FCSTD DOCUMENT  (FreeCAD 0.16R6706 (Git))
Label: coxa
License: All rights reserved
LicenseURL: http://en.wikipedia.org/wiki/All_rights_reserved
objects: Sketcher::SketchObject×3
note: 3 computed .brp shape members not serialized (recipe doc carries the construction recipe); baked Part::Feature solids carry a one-line shape summary decoded from their .brp

FEATURE [Sketcher::SketchObject] Sketch  label="coxa_up"
  sketch-geometry (27):
    g0: LineSegment StartX=38.0826 StartY=27.4348 StartZ=0 EndX=51.0826 EndY=27.4348 EndZ=0
    g1: LineSegment StartX=38.0826 StartY=11.9348 StartZ=0 EndX=51.0826 EndY=11.9348 EndZ=0
    g2: LineSegment StartX=65.8826 StartY=27.4348 StartZ=0 EndX=65.8826 EndY=30.4348 EndZ=0
    g3: LineSegment StartX=65.8826 StartY=30.4348 StartZ=0 EndX=68.8826 EndY=30.4348 EndZ=0
    g4: LineSegment StartX=68.8826 StartY=30.4348 StartZ=0 EndX=68.8826 EndY=8.93483 EndZ=0
    g5: LineSegment StartX=68.8826 StartY=8.93483 StartZ=0 EndX=65.8826 EndY=8.93483 EndZ=0
    g6: LineSegment StartX=65.8826 StartY=8.93483 StartZ=0 EndX=65.8826 EndY=11.9348 EndZ=0
    g7: LineSegment StartX=65.8826 StartY=11.9348 StartZ=0 EndX=54.0826 EndY=11.9348 EndZ=0
    g8: LineSegment StartX=54.0826 StartY=11.9348 StartZ=0 EndX=54.0826 EndY=8.93483 EndZ=0
    g9: LineSegment StartX=54.0826 StartY=8.93483 StartZ=0 EndX=51.0826 EndY=8.93483 EndZ=0
    g10: LineSegment StartX=51.0826 StartY=8.93483 StartZ=0 EndX=51.0826 EndY=11.9348 EndZ=0
    g11: LineSegment StartX=51.0826 StartY=27.4348 StartZ=0 EndX=51.0826 EndY=30.4348 EndZ=0
    g12: LineSegment StartX=51.0826 StartY=30.4348 StartZ=0 EndX=54.0826 EndY=30.4348 EndZ=0
    g13: LineSegment StartX=54.0826 StartY=30.4348 StartZ=0 EndX=54.0826 EndY=27.4348 EndZ=0
    g14: LineSegment StartX=54.0826 StartY=27.4348 StartZ=0 EndX=65.8826 EndY=27.4348 EndZ=0
    g15: GeomPoint [constr] X=68.8826 Y=19.6848 Z=0
    g16: LineSegment [constr] StartX=68.8826 StartY=19.6848 StartZ=0 EndX=38.0826 EndY=19.6848 EndZ=0
    g17: ArcOfEllipse CenterX=38.0826 CenterY=19.6848 CenterZ=0 NormalX=0 NormalY=0 NormalZ=1 MajorRadius=11 MinorRadius=7.75 AngleXU=0 StartAngle=1.5708 EndAngle=4.71239
    g18: LineSegment [constr] StartX=49.0826 StartY=19.6848 StartZ=0 EndX=27.0826 EndY=19.6848 EndZ=0
    g19: LineSegment [constr] StartX=38.0826 StartY=27.4348 StartZ=0 EndX=38.0826 EndY=11.9348 EndZ=0
    g20: GeomPoint [constr] X=45.8888 Y=19.6848 Z=0
    g21: GeomPoint [constr] X=30.2764 Y=19.6848 Z=0
    g22: Circle CenterX=38.0826 CenterY=19.6848 CenterZ=0 NormalX=0 NormalY=0 NormalZ=1 Radius=3.5
    g23: Circle CenterX=31.0826 CenterY=19.6848 CenterZ=0 NormalX=0 NormalY=0 NormalZ=1 Radius=1.2
    g24: Circle CenterX=45.0826 CenterY=19.6848 CenterZ=0 NormalX=0 NormalY=0 NormalZ=1 Radius=1.2
    g25: GeomPoint [constr] X=59.9826 Y=27.4348 Z=0
    g26: LineSegment [constr] StartX=59.9826 StartY=27.4348 StartZ=0 EndX=59.9826 EndY=11.9348 EndZ=0
  constraints (66):
    c: Horizontal(g0)
    c: Horizontal(g1)
    c: Vertical(g2)
    c: Distance(g2,g0) = 3
    c: Coincident(g3,g2)
    c: Horizontal(g3)
    c: Distance(g3,g2) = 3
    c: Coincident(g4,g3)
    c: Vertical(g4)
    c: Horizontal(g5)
    c: Coincident(g6,g5)
    c: Vertical(g6)
    c: Horizontal(g7)
    c: Distance(g7,g6) = 11.8
    c: Vertical(g8)
    c: Coincident(g9,g8)
    c: Horizontal(g9)
    c: Distance(g9,g8) = 3
    c: Coincident(g10,g9)
    c: Vertical(g10)
    c: Coincident(g7,g8)
    c: Distance(g8,g7) = 3
    c: Distance(g5,g7) = 3
    c: Coincident(g1,g10)
    c: Vertical(g11)
    c: Coincident(g12,g11)
    c: Horizontal(g12)
    c: Distance(g12,g11) = 3
    c: Coincident(g13,g12)
    c: Vertical(g13)
    c: Coincident(g11,g0)
    c: Distance(g13,g2) = 11.8
    c: Coincident(g6,g7)
    c: Distance(g11,g0) = 3
    c: Coincident(g14,g13)
    c: Coincident(g14,g2)
    c: Horizontal(g14)
    c: Distance(g12,g14) = 3
    c: Distance(g9,g1) = 3
    c: Coincident(g16,g15)
    c: Horizontal(g16)
    c: InternalAlignment(g18-g21 -> g17) x4
    c: Coincident(g17,g16)
    c: Coincident(g0,g19)
    c: Coincident(g1,g19)
    c: Vertical(g19)
    c: PointOnObject(g17,g19)
    c: PointOnObject(g17,g19)
    c: Radius(g22) = 3.5
    c: PointOnObject(g23,g18)
    c: Radius(g23) = 1.2
    c: Coincident(g16,g22)
    c: Distance(g23,g16) = 7
    c: PointOnObject(g24,g16)
    c: Radius(g24) = 1.2
    c: Distance(g24,g16) = 7
    c: Symmetric(g13,g2,g25)
    c: Coincident(g26,g25)
    c: PointOnObject(g26,g7)
    c: Vertical(g26)
    c: Coincident(g4,g5)
    c: Distance(g6,g4) = 3
    c: PointOnObject(g15,g4)
    c: Distance(g13,g7) = 15.5
    c: Distance(g23,g18) = 4
    c: Distance(g0,g0) = 13
FEATURE [Sketcher::SketchObject] Sketch005  label="coxa_down"
  sketch-geometry (23):
    g0: LineSegment StartX=66.5079 StartY=3.73245 StartZ=0 EndX=66.5079 EndY=6.73245 EndZ=0
    g1: LineSegment StartX=66.5079 StartY=6.73245 StartZ=0 EndX=69.5079 EndY=6.73245 EndZ=0
    g2: LineSegment StartX=69.5079 StartY=6.73245 StartZ=0 EndX=69.5079 EndY=-14.7675 EndZ=0
    g3: LineSegment StartX=69.5079 StartY=-14.7675 StartZ=0 EndX=66.5079 EndY=-14.7675 EndZ=0
    g4: LineSegment StartX=66.5079 StartY=-14.7675 StartZ=0 EndX=66.5079 EndY=-11.7675 EndZ=0
    g5: LineSegment StartX=66.5079 StartY=-11.7675 StartZ=0 EndX=54.7079 EndY=-11.7675 EndZ=0
    g6: LineSegment StartX=54.7079 StartY=-11.7675 StartZ=0 EndX=54.7079 EndY=-14.7675 EndZ=0
    g7: LineSegment StartX=54.7079 StartY=-14.7675 StartZ=0 EndX=51.7079 EndY=-14.7675 EndZ=0
    g8: LineSegment StartX=51.7079 StartY=-14.7675 StartZ=0 EndX=51.7079 EndY=-11.7675 EndZ=0
    g9: LineSegment StartX=51.7079 StartY=3.73245 StartZ=0 EndX=51.7079 EndY=6.73245 EndZ=0
    g10: LineSegment StartX=51.7079 StartY=6.73245 StartZ=0 EndX=54.7079 EndY=6.73245 EndZ=0
    g11: LineSegment StartX=54.7079 StartY=6.73245 StartZ=0 EndX=54.7079 EndY=3.73245 EndZ=0
    g12: LineSegment StartX=54.7079 StartY=3.73245 StartZ=0 EndX=66.5079 EndY=3.73245 EndZ=0
    g13: GeomPoint [constr] X=51.7079 Y=3.73245 Z=0
    g14: LineSegment [constr] StartX=69.5079 StartY=-4.01755 StartZ=0 EndX=38.7079 EndY=-4.01755 EndZ=0
    g15: Circle CenterX=38.7079 CenterY=-4.01755 CenterZ=0 NormalX=0 NormalY=0 NormalZ=1 Radius=1.5
    g16: LineSegment [constr] StartX=51.7079 StartY=3.73245 StartZ=0 EndX=51.7079 EndY=-4.01755 EndZ=0
    g17: ArcOfEllipse CenterX=51.7079 CenterY=-4.01755 CenterZ=0 NormalX=0 NormalY=0 NormalZ=1 MajorRadius=17 MinorRadius=7.75 AngleXU=0 StartAngle=1.5708 EndAngle=4.71239
    g18: LineSegment [constr] StartX=68.7079 StartY=-4.01755 StartZ=0 EndX=34.7079 EndY=-4.01755 EndZ=0
    g19: LineSegment [constr] StartX=51.7079 StartY=3.73245 StartZ=0 EndX=51.7079 EndY=-11.7675 EndZ=0
    g20: GeomPoint [constr] X=36.5772 Y=-4.01755 Z=0
    g21: GeomPoint [constr] X=60.6079 Y=3.73245 Z=0
    g22: LineSegment [constr] StartX=60.6079 StartY=3.73245 StartZ=0 EndX=60.6079 EndY=-11.7675 EndZ=0
  constraints (66):
    c: Vertical(g0)
    c: Coincident(g1,g0)
    c: Horizontal(g1)
    c: Distance(g1,g0) = 3
    c: Vertical(g2)
    c: Horizontal(g3)
    c: Distance(g3,g2) = 3
    c: Coincident(g4,g3)
    c: Vertical(g4)
    c: Horizontal(g5)
    c: Distance(g5,g4) = 11.8
    c: Vertical(g6)
    c: Coincident(g7,g6)
    c: Horizontal(g7)
    c: Distance(g7,g6) = 3
    c: Coincident(g8,g7)
    c: Vertical(g8)
    c: Coincident(g5,g6)
    c: Distance(g6,g5) = 3
    c: Distance(g3,g5) = 3
    c: Vertical(g9)
    c: Coincident(g10,g9)
    c: Horizontal(g10)
    c: Distance(g10,g9) = 3
    c: Coincident(g11,g10)
    c: Vertical(g11)
    c: Distance(g11,g0) = 11.8
    c: Coincident(g4,g5)
    c: Coincident(g12,g0)
    c: Distance(g10,g12) = 3
    c: Coincident(g3,g2)
    c: Horizontal(g14)
    c: Radius(g15) = 1.5
    c: Coincident(g14,g15)
    c: Coincident(g16,g13)
    c: PointOnObject(g16,g14)
    c: Vertical(g16)
    c: InternalAlignment(g18,g17)
    c: InternalAlignment(g19,g17)
    c: InternalAlignment(g20,g17)
    c: Coincident(g19,g13)
    c: Vertical(g19)
    c: PointOnObject(g17,g16)
    c: PointOnObject(g17,g19)
    c: Tangent(g17,g17)
    c: PointOnObject(g16,g18)
    c: Tangent(g17,g17)
    c: PointOnObject(g8,g5)
    c: Distance(g14,g16) = 13
    c: PointOnObject(g10,g1)
    c: Symmetric(g11,g0,g21)
    c: PointOnObject(g12,g11)
    c: Coincident(g22,g21)
    c: PointOnObject(g22,g5)
    c: Vertical(g22)
    c: Tangent(g17,g17)
    c: Horizontal(g12)
    c: Coincident(g1,g2)
    c: PointOnObject(g14,g2)
    c: PointOnObject(g9,g12)
    c: PointOnObject(g11,g12)
    c: Distance(g11,g5) = 15.5
    c: PointOnObject(g13,g12)
    c: PointOnObject(g13,g9)
    c: PointOnObject(g17,g5)
    c: Distance(g14,g18) = 4
FEATURE [Sketcher::SketchObject] Sketch006  label="coxa_joint"
  sketch-geometry (35):
    g0: LineSegment StartX=97.0509 StartY=-32.2316 StartZ=0 EndX=85.2509 EndY=-32.2316 EndZ=0
    g1: LineSegment StartX=85.2509 StartY=-32.2316 StartZ=0 EndX=85.2509 EndY=-54.7316 EndZ=0
    g2: LineSegment StartX=85.2509 StartY=-54.7316 StartZ=0 EndX=97.0509 EndY=-54.7316 EndZ=0
    g3: LineSegment StartX=97.0509 StartY=-54.7316 StartZ=0 EndX=97.0509 EndY=-32.2316 EndZ=0
    g4: Circle CenterX=91.1509 CenterY=-29.2316 CenterZ=0 NormalX=0 NormalY=0 NormalZ=1 Radius=1.5
    g5: Circle CenterX=91.1509 CenterY=-57.7316 CenterZ=0 NormalX=0 NormalY=0 NormalZ=1 Radius=1.5
    g6: LineSegment StartX=97.0509 StartY=-23.2316 StartZ=0 EndX=100.051 EndY=-23.2316 EndZ=0
    g7: LineSegment StartX=100.051 StartY=-26.2316 StartZ=0 EndX=97.0509 EndY=-26.2316 EndZ=0
    g8: LineSegment StartX=97.0509 StartY=-26.2316 StartZ=0 EndX=97.0509 EndY=-23.2316 EndZ=0
    g9: LineSegment StartX=82.2509 StartY=-23.2316 StartZ=0 EndX=85.2509 EndY=-23.2316 EndZ=0
    g10: LineSegment StartX=85.2509 StartY=-23.2316 StartZ=0 EndX=85.2509 EndY=-26.2316 EndZ=0
    g11: LineSegment StartX=85.2509 StartY=-26.2316 StartZ=0 EndX=82.2509 EndY=-26.2316 EndZ=0
    g12: LineSegment StartX=97.0509 StartY=-60.7316 StartZ=0 EndX=100.051 EndY=-60.7316 EndZ=0
    g13: LineSegment StartX=100.051 StartY=-63.7316 StartZ=0 EndX=97.0509 EndY=-63.7316 EndZ=0
    g14: LineSegment StartX=97.0509 StartY=-63.7316 StartZ=0 EndX=97.0509 EndY=-60.7316 EndZ=0
    g15: LineSegment StartX=82.2509 StartY=-60.7316 StartZ=0 EndX=85.2509 EndY=-60.7316 EndZ=0
    g16: LineSegment StartX=85.2509 StartY=-60.7316 StartZ=0 EndX=85.2509 EndY=-63.7316 EndZ=0
    g17: LineSegment StartX=85.2509 StartY=-63.7316 StartZ=0 EndX=82.2509 EndY=-63.7316 EndZ=0
    g18: LineSegment StartX=85.2509 StartY=-20.2316 StartZ=0 EndX=97.0509 EndY=-20.2316 EndZ=0
    g19: LineSegment StartX=97.0509 StartY=-66.7316 StartZ=0 EndX=85.2509 EndY=-66.7316 EndZ=0
    g20: LineSegment [constr] StartX=85.2509 StartY=-32.2316 StartZ=0 EndX=97.0509 EndY=-32.2316 EndZ=0
    g21: LineSegment [constr] StartX=97.0509 StartY=-32.2316 StartZ=0 EndX=97.0509 EndY=-27.5316 EndZ=0
    g22: LineSegment [constr] StartX=97.0509 StartY=-27.5316 StartZ=0 EndX=85.2509 EndY=-27.5316 EndZ=0
    g23: LineSegment [constr] StartX=85.2509 StartY=-27.5316 StartZ=0 EndX=85.2509 EndY=-32.2316 EndZ=0
    g24: LineSegment [constr] StartX=91.1509 StartY=-29.2316 StartZ=0 EndX=91.1509 EndY=-57.7316 EndZ=0
    g25: GeomPoint [constr] X=91.1509 Y=-32.2316 Z=0
    g26: LineSegment [constr] StartX=100.051 StartY=-23.2316 StartZ=0 EndX=100.051 EndY=-63.7316 EndZ=0
    g27: ArcOfCircle CenterX=97.0509 CenterY=-23.2316 CenterZ=0 NormalX=0 NormalY=0 NormalZ=1 Radius=3 StartAngle=0 EndAngle=1.5708
    g28: ArcOfCircle CenterX=97.0509 CenterY=-63.7316 CenterZ=0 NormalX=0 NormalY=0 NormalZ=1 Radius=3 StartAngle=4.71239 EndAngle=6.28319
    g29: LineSegment StartX=100.051 StartY=-26.2316 StartZ=0 EndX=100.051 EndY=-60.7316 EndZ=0
    g30: LineSegment [constr] StartX=82.2509 StartY=-63.7316 StartZ=0 EndX=82.2509 EndY=-23.2316 EndZ=0
    g31: ArcOfCircle CenterX=85.2509 CenterY=-63.7316 CenterZ=0 NormalX=0 NormalY=0 NormalZ=1 Radius=3 StartAngle=3.14159 EndAngle=4.71239
    g32: ArcOfCircle CenterX=85.2509 CenterY=-23.2316 CenterZ=0 NormalX=0 NormalY=0 NormalZ=1 Radius=3 StartAngle=1.5708 EndAngle=3.14159
    g33: LineSegment StartX=82.2509 StartY=-26.2316 StartZ=0 EndX=82.2509 EndY=-60.7316 EndZ=0
    g34: GeomPoint [constr] X=91.1509 Y=-38.1316 Z=0
  constraints (101):
    c: Coincident(g0,g1)
    c: Coincident(g1,g2)
    c: Coincident(g2,g3)
    c: Coincident(g3,g0)
    c: Horizontal(g0)
    c: Horizontal(g2)
    c: Vertical(g1)
    c: Vertical(g3)
    c: Distance(g0,g3) = 11.8
    c: Distance(g0,g2) = 22.5
    c: Radius(g4) = 1.5
    c: Distance(g4,g0) = 3
    c: Radius(g5) = 1.5
    c: Distance(g5,g2) = 3
    c: Coincident(g7,g8)
    c: Coincident(g8,g6)
    c: Horizontal(g6)
    c: Horizontal(g7)
    c: Vertical(g8)
    c: Distance(g7,g6) = 3
    c: Coincident(g9,g10)
    c: Coincident(g10,g11)
    c: Horizontal(g9)
    c: Horizontal(g11)
    c: Vertical(g10)
    c: Distance(g10,g9) = 3
    c: Distance(g11,g10) = 3
    c: PointOnObject(g7,g3)
    c: PointOnObject(g10,g1)
    c: Distance(g7,g0) = 6
    c: Distance(g10,g0) = 6
    c: Coincident(g13,g14)
    c: Coincident(g14,g12)
    c: Horizontal(g12)
    c: Horizontal(g13)
    c: Vertical(g14)
    c: Distance(g13,g12) = 3
    c: PointOnObject(g12,g3)
    c: Distance(g12,g2) = 6
    c: Coincident(g15,g16)
    c: Coincident(g16,g17)
    c: Horizontal(g15)
    c: Horizontal(g17)
    c: Vertical(g16)
    c: Distance(g16,g15) = 3
    c: Distance(g17,g16) = 3
    c: PointOnObject(g15,g1)
    c: Distance(g15,g2) = 6
    c: Horizontal(g18)
    c: Horizontal(g19)
    c: Distance(g9,g18) = 3
    c: Distance(g13,g19) = 3
    c: Coincident(g20,g21)
    c: Coincident(g21,g22)
    c: Coincident(g22,g23)
    c: Coincident(g23,g20)
    c: Horizontal(g20)
    c: Horizontal(g22)
    c: Vertical(g21)
    c: Vertical(g23)
    c: Coincident(g20,g0)
    c: PointOnObject(g21,g3)
    c: Distance(g21,g0) = 4.7
    c: Coincident(g24,g4)
    c: Coincident(g24,g5)
    c: Vertical(g24)
    c: PointOnObject(g25,g24)
    c: Symmetric(g0,g0,g25)
    c: Coincident(g26,g6)
    c: Coincident(g26,g13)
    c: Vertical(g26)
    c: PointOnObject(g12,g26)
    c: Distance(g13,g26) = 3
    c: PointOnObject(g7,g26)
    c: PointOnObject(g27,g6)
    c: Coincident(g27,g18)
    c: Coincident(g27,g6)
    c: Radius(g27) = 3
    c: PointOnObject(g28,g13)
    c: Coincident(g28,g19)
    c: Coincident(g28,g13)
    c: Radius(g28) = 3
    c: Coincident(g29,g7)
    c: Coincident(g29,g12)
    c: Coincident(g30,g17)
    c: Coincident(g30,g9)
    c: Vertical(g30)
    c: PointOnObject(g15,g30)
    c: PointOnObject(g31,g17)
    c: Coincident(g31,g19)
    c: Coincident(g31,g17)
    c: Radius(g31) = 3
    c: PointOnObject(g32,g9)
    c: Coincident(g32,g18)
    c: Coincident(g32,g9)
    c: Radius(g32) = 3
    c: Coincident(g33,g15)
    c: Vertical(g33)
    c: PointOnObject(g33,g11)
    c: PointOnObject(g34,g24)
    c: Distance(g34,g0) = 5.9
